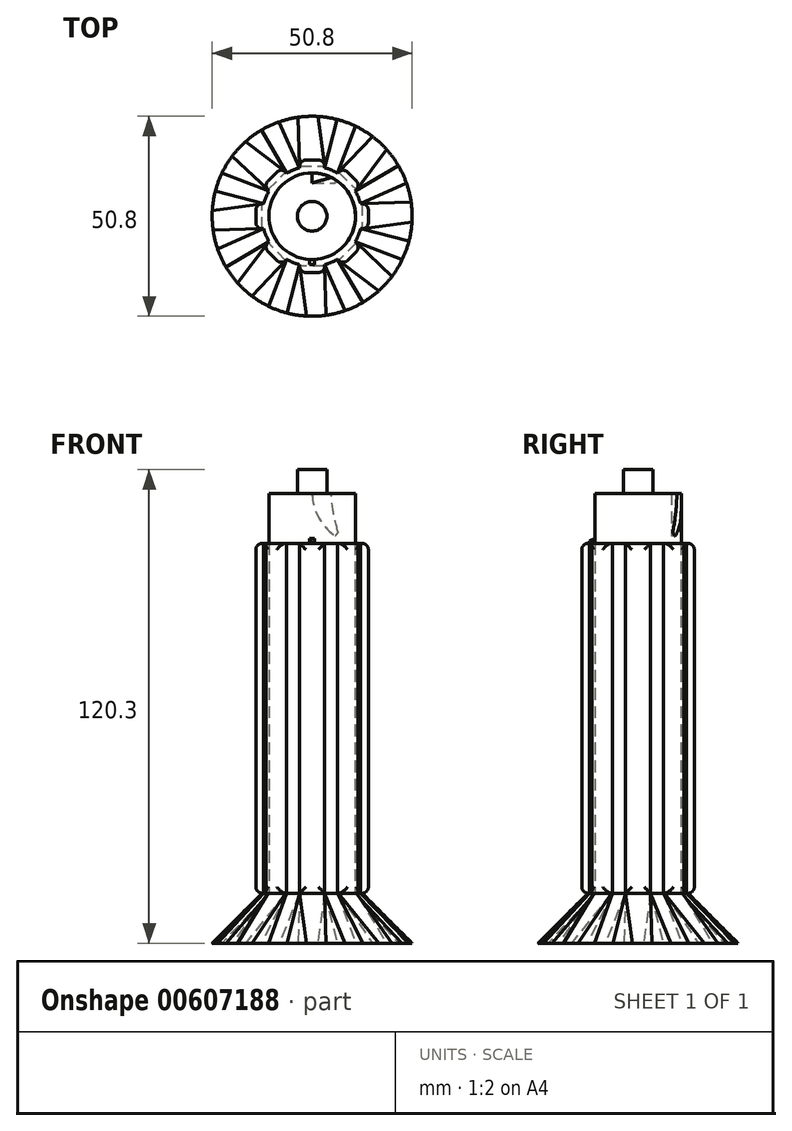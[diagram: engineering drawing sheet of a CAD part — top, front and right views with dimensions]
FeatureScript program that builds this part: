
annotation { "Feature Type Name" : "Feature", "Feature Type Description" : "" }
export const myFeature = defineFeature(function(context is Context, id is Id, definition is map)
    precondition{}
    {
        {
            var Q0;
            Q0=qCreatedBy(makeId("Top.planeOp"),FACE);
            var sketch = newSketch(context, id + "F0", { "sketchPlane" : qUnion([Q0])});
            skCircle(sketch, "E0", {"center": v(0, 0) * mm, "radius": 12.7 * mm});
            skLineSegment(sketch, "E1.bottom", {"start": v(-3.18, 14.29) * mm, "end": v(3.18, 14.29) * mm});
            skLineSegment(sketch, "E1.top", {"start": v(-3.18, 11.11) * mm, "end": v(3.18, 11.11) * mm});
            skLineSegment(sketch, "E1.left", {"start": v(-3.18, 14.29) * mm, "end": v(-3.18, 11.11) * mm});
            skLineSegment(sketch, "E1.right", {"start": v(3.18, 14.29) * mm, "end": v(3.18, 11.11) * mm});
            skLineSegment(sketch, "E2.1.0", {"start": v(-12.35, 7.86) * mm, "end": v(-7.86, 12.35) * mm});
            skLineSegment(sketch, "E2.1.1", {"start": v(-7.86, 12.35) * mm, "end": v(-5.61, 10.1) * mm});
            skLineSegment(sketch, "E2.1.2", {"start": v(-12.35, 7.86) * mm, "end": v(-10.1, 5.61) * mm});
            skLineSegment(sketch, "E2.1.3", {"start": v(-10.1, 5.61) * mm, "end": v(-5.61, 10.1) * mm});
            skLineSegment(sketch, "E2.2.0", {"start": v(-14.29, -3.17) * mm, "end": v(-14.29, 3.18) * mm});
            skLineSegment(sketch, "E2.2.1", {"start": v(-14.29, 3.18) * mm, "end": v(-11.11, 3.18) * mm});
            skLineSegment(sketch, "E2.2.2", {"start": v(-14.29, -3.17) * mm, "end": v(-11.11, -3.17) * mm});
            skLineSegment(sketch, "E2.2.3", {"start": v(-11.11, -3.17) * mm, "end": v(-11.11, 3.18) * mm});
            skLineSegment(sketch, "E2.3.0", {"start": v(-7.86, -12.35) * mm, "end": v(-12.35, -7.86) * mm});
            skLineSegment(sketch, "E2.3.1", {"start": v(-12.35, -7.86) * mm, "end": v(-10.1, -5.61) * mm});
            skLineSegment(sketch, "E2.3.2", {"start": v(-7.86, -12.35) * mm, "end": v(-5.61, -10.1) * mm});
            skLineSegment(sketch, "E2.3.3", {"start": v(-5.61, -10.1) * mm, "end": v(-10.1, -5.61) * mm});
            skLineSegment(sketch, "E2.4.0", {"start": v(3.17, -14.29) * mm, "end": v(-3.18, -14.29) * mm});
            skLineSegment(sketch, "E2.4.1", {"start": v(-3.18, -14.29) * mm, "end": v(-3.18, -11.11) * mm});
            skLineSegment(sketch, "E2.4.2", {"start": v(3.17, -14.29) * mm, "end": v(3.17, -11.11) * mm});
            skLineSegment(sketch, "E2.4.3", {"start": v(3.17, -11.11) * mm, "end": v(-3.18, -11.11) * mm});
            skLineSegment(sketch, "E2.5.0", {"start": v(12.35, -7.86) * mm, "end": v(7.86, -12.35) * mm});
            skLineSegment(sketch, "E2.5.1", {"start": v(7.86, -12.35) * mm, "end": v(5.61, -10.1) * mm});
            skLineSegment(sketch, "E2.5.2", {"start": v(12.35, -7.86) * mm, "end": v(10.1, -5.61) * mm});
            skLineSegment(sketch, "E2.5.3", {"start": v(10.1, -5.61) * mm, "end": v(5.61, -10.1) * mm});
            skLineSegment(sketch, "E2.6.0", {"start": v(14.29, 3.17) * mm, "end": v(14.29, -3.18) * mm});
            skLineSegment(sketch, "E2.6.1", {"start": v(14.29, -3.18) * mm, "end": v(11.11, -3.18) * mm});
            skLineSegment(sketch, "E2.6.2", {"start": v(14.29, 3.17) * mm, "end": v(11.11, 3.17) * mm});
            skLineSegment(sketch, "E2.6.3", {"start": v(11.11, 3.17) * mm, "end": v(11.11, -3.18) * mm});
            skLineSegment(sketch, "E2.7.0", {"start": v(7.86, 12.35) * mm, "end": v(12.35, 7.86) * mm});
            skLineSegment(sketch, "E2.7.1", {"start": v(12.35, 7.86) * mm, "end": v(10.1, 5.61) * mm});
            skLineSegment(sketch, "E2.7.2", {"start": v(7.86, 12.35) * mm, "end": v(5.61, 10.1) * mm});
            skLineSegment(sketch, "E2.7.3", {"start": v(5.61, 10.1) * mm, "end": v(10.1, 5.61) * mm});
            skSolve(sketch);
        }
        {
            var Q0;
            {var subQ5=sQuery(id+"F0.wireOp",EDGE,"E2.1.0");Q0=makeQuery(id+"F0.imprint","IMPRINT",FACE,{"disambiguationData":[TD([[makeQuery(id+"F0.imprint","IMPRINT",EDGE,{"derivedFrom":subQ5}),-1.0]])]});}
            var Q1;
            {var subQ5=sQuery(id+"F0.wireOp",EDGE,"E2.1.3");Q1=makeQuery(id+"F0.imprint","IMPRINT",FACE,{"disambiguationData":[TD([[makeQuery(id+"F0.imprint","IMPRINT",EDGE,{"derivedFrom":subQ5}),1.0]])]});}
            var Q2;
            {var subQ20=sQuery(id+"F0.wireOp",EDGE,"E1.top");Q2=makeQuery(id+"F0.imprint","IMPRINT",FACE,{"disambiguationData":[TD([[makeQuery(id+"F0.imprint","IMPRINT",EDGE,{"derivedFrom":subQ20}),-1.0]])]});}
            var Q3;
            {var subQ5=sQuery(id+"F0.wireOp",EDGE,"E1.top");Q3=makeQuery(id+"F0.imprint","IMPRINT",FACE,{"disambiguationData":[TD([[makeQuery(id+"F0.imprint","IMPRINT",EDGE,{"derivedFrom":subQ5}),1.0]])]});}
            var Q4;
            {var subQ5=sQuery(id+"F0.wireOp",EDGE,"E1.bottom");Q4=makeQuery(id+"F0.imprint","IMPRINT",FACE,{"disambiguationData":[TD([[makeQuery(id+"F0.imprint","IMPRINT",EDGE,{"derivedFrom":subQ5}),-1.0]])]});}
            var Q5;
            {var subQ5=sQuery(id+"F0.wireOp",EDGE,"E2.7.0");Q5=makeQuery(id+"F0.imprint","IMPRINT",FACE,{"disambiguationData":[TD([[makeQuery(id+"F0.imprint","IMPRINT",EDGE,{"derivedFrom":subQ5}),-1.0]])]});}
            var Q6;
            {var subQ5=sQuery(id+"F0.wireOp",EDGE,"E2.7.3");Q6=makeQuery(id+"F0.imprint","IMPRINT",FACE,{"disambiguationData":[TD([[makeQuery(id+"F0.imprint","IMPRINT",EDGE,{"derivedFrom":subQ5}),1.0]])]});}
            var Q7;
            {var subQ5=sQuery(id+"F0.wireOp",EDGE,"E2.6.3");Q7=makeQuery(id+"F0.imprint","IMPRINT",FACE,{"disambiguationData":[TD([[makeQuery(id+"F0.imprint","IMPRINT",EDGE,{"derivedFrom":subQ5}),1.0]])]});}
            var Q8;
            {var subQ5=sQuery(id+"F0.wireOp",EDGE,"E2.6.0");Q8=makeQuery(id+"F0.imprint","IMPRINT",FACE,{"disambiguationData":[TD([[makeQuery(id+"F0.imprint","IMPRINT",EDGE,{"derivedFrom":subQ5}),-1.0]])]});}
            var Q9;
            {var subQ5=sQuery(id+"F0.wireOp",EDGE,"E2.5.3");Q9=makeQuery(id+"F0.imprint","IMPRINT",FACE,{"disambiguationData":[TD([[makeQuery(id+"F0.imprint","IMPRINT",EDGE,{"derivedFrom":subQ5}),1.0]])]});}
            var Q10;
            {var subQ5=sQuery(id+"F0.wireOp",EDGE,"E2.5.0");Q10=makeQuery(id+"F0.imprint","IMPRINT",FACE,{"disambiguationData":[TD([[makeQuery(id+"F0.imprint","IMPRINT",EDGE,{"derivedFrom":subQ5}),-1.0]])]});}
            var Q11;
            {var subQ5=sQuery(id+"F0.wireOp",EDGE,"E2.4.3");Q11=makeQuery(id+"F0.imprint","IMPRINT",FACE,{"disambiguationData":[TD([[makeQuery(id+"F0.imprint","IMPRINT",EDGE,{"derivedFrom":subQ5}),1.0]])]});}
            var Q12;
            {var subQ5=sQuery(id+"F0.wireOp",EDGE,"E2.4.0");Q12=makeQuery(id+"F0.imprint","IMPRINT",FACE,{"disambiguationData":[TD([[makeQuery(id+"F0.imprint","IMPRINT",EDGE,{"derivedFrom":subQ5}),-1.0]])]});}
            var Q13;
            {var subQ5=sQuery(id+"F0.wireOp",EDGE,"E2.3.3");Q13=makeQuery(id+"F0.imprint","IMPRINT",FACE,{"disambiguationData":[TD([[makeQuery(id+"F0.imprint","IMPRINT",EDGE,{"derivedFrom":subQ5}),1.0]])]});}
            var Q14;
            {var subQ5=sQuery(id+"F0.wireOp",EDGE,"E2.3.0");Q14=makeQuery(id+"F0.imprint","IMPRINT",FACE,{"disambiguationData":[TD([[makeQuery(id+"F0.imprint","IMPRINT",EDGE,{"derivedFrom":subQ5}),-1.0]])]});}
            var Q15;
            {var subQ5=sQuery(id+"F0.wireOp",EDGE,"E2.2.3");Q15=makeQuery(id+"F0.imprint","IMPRINT",FACE,{"disambiguationData":[TD([[makeQuery(id+"F0.imprint","IMPRINT",EDGE,{"derivedFrom":subQ5}),1.0]])]});}
            var Q16;
            {var subQ5=sQuery(id+"F0.wireOp",EDGE,"E2.2.0");Q16=makeQuery(id+"F0.imprint","IMPRINT",FACE,{"disambiguationData":[TD([[makeQuery(id+"F0.imprint","IMPRINT",EDGE,{"derivedFrom":subQ5}),-1.0]])]});}
            extrude(context, id + "F1", {"entities" : qUnion([Q0, Q1, Q2, Q3, Q4, Q5, Q6, Q7, Q8, Q9, Q10, Q11, Q12, Q13, Q14, Q15, Q16]), "depth" : 88.9 * mm, "offsetDistance" : 25.4 * mm});
        }
        {
            var Q0;
            Q0=makeQuery(id+"F1.opExtrude","CAP_FACE",FACE,{"disambiguationData":[OSD([sQuery(id+"F0.wireOp",EDGE,"E0"),sQuery(id+"F0.wireOp",EDGE,"E1.bottom"),sQuery(id+"F0.wireOp",EDGE,"E1.left"),sQuery(id+"F0.wireOp",EDGE,"E1.right"),sQuery(id+"F0.wireOp",EDGE,"E2.1.0"),sQuery(id+"F0.wireOp",EDGE,"E2.1.1"),sQuery(id+"F0.wireOp",EDGE,"E2.1.2"),sQuery(id+"F0.wireOp",EDGE,"E2.2.0"),sQuery(id+"F0.wireOp",EDGE,"E2.2.1"),sQuery(id+"F0.wireOp",EDGE,"E2.2.2"),sQuery(id+"F0.wireOp",EDGE,"E2.3.0"),sQuery(id+"F0.wireOp",EDGE,"E2.3.1"),sQuery(id+"F0.wireOp",EDGE,"E2.3.2"),sQuery(id+"F0.wireOp",EDGE,"E2.4.0"),sQuery(id+"F0.wireOp",EDGE,"E2.4.1"),sQuery(id+"F0.wireOp",EDGE,"E2.4.2"),sQuery(id+"F0.wireOp",EDGE,"E2.5.0"),sQuery(id+"F0.wireOp",EDGE,"E2.5.1"),sQuery(id+"F0.wireOp",EDGE,"E2.5.2"),sQuery(id+"F0.wireOp",EDGE,"E2.6.0"),sQuery(id+"F0.wireOp",EDGE,"E2.6.1"),sQuery(id+"F0.wireOp",EDGE,"E2.6.2"),sQuery(id+"F0.wireOp",EDGE,"E2.7.0"),sQuery(id+"F0.wireOp",EDGE,"E2.7.1"),sQuery(id+"F0.wireOp",EDGE,"E2.7.2")])],"isStart":true});
            cPlane(context, id + "F2", {"entities" : qUnion([Q0]), "cplaneType" : CPlaneType.OFFSET, "offset" : 12.7 * mm, "width" : 152.4 * mm, "height" : 152.4 * mm});
        }
        {
            var Q0;
            Q0=qCreatedBy(id+"F2.planeOp",FACE);
            var sketch = newSketch(context, id + "F3", { "sketchPlane" : qUnion([Q0])});
            skCircle(sketch, "E3", {"center": v(0, 0) * mm, "radius": 25.4 * mm});
            skSolve(sketch);
        }
        {
            var Q0;
            Q0=makeQuery(id+"F1.opExtrude","SWEPT_FACE",FACE,{"disambiguationData":[OSD([sQuery(id+"F0.wireOp",EDGE,"E1.bottom")])]});
            var Q1;
            Q1=makeQuery(id+"F1.opExtrude","SWEPT_FACE",FACE,{"disambiguationData":[OSD([sQuery(id+"F0.wireOp",EDGE,"E2.1.0")])]});
            var Q2;
            Q2=makeQuery(id+"F1.opExtrude","SWEPT_FACE",FACE,{"disambiguationData":[OSD([sQuery(id+"F0.wireOp",EDGE,"E2.7.0")])]});
            var Q3;
            Q3=makeQuery(id+"F1.opExtrude","SWEPT_FACE",FACE,{"disambiguationData":[OSD([sQuery(id+"F0.wireOp",EDGE,"E2.6.0")])]});
            var Q4;
            Q4=makeQuery(id+"F1.opExtrude","SWEPT_FACE",FACE,{"disambiguationData":[OSD([sQuery(id+"F0.wireOp",EDGE,"E2.5.0")])]});
            var Q5;
            Q5=makeQuery(id+"F1.opExtrude","SWEPT_FACE",FACE,{"disambiguationData":[OSD([sQuery(id+"F0.wireOp",EDGE,"E2.4.0")])]});
            var Q6;
            Q6=makeQuery(id+"F1.opExtrude","SWEPT_FACE",FACE,{"disambiguationData":[OSD([sQuery(id+"F0.wireOp",EDGE,"E2.3.0")])]});
            var Q7;
            Q7=makeQuery(id+"F1.opExtrude","SWEPT_FACE",FACE,{"disambiguationData":[OSD([sQuery(id+"F0.wireOp",EDGE,"E2.2.0")])]});
            var Q8;
            Q8=makeQuery(id+"F1.opExtrude","CAP_EDGE",EDGE,{"disambiguationData":[OSD([sQuery(id+"F0.wireOp",EDGE,"E2.3.0")])],"isStart":true});
            fillet(context, id + "F4", {"entities" : qUnion([Q0, Q1, Q2, Q3, Q4, Q5, Q6, Q7, Q8]), "radius" : 1.59 * mm, "tangentPropagation" : true, "allowEdgeOverflow" : false});
        }
        {
            var Q1;
            Q1=makeQuery(id+"F1.opExtrude","CAP_FACE",FACE,{"disambiguationData":[OSD([sQuery(id+"F0.wireOp",EDGE,"E0"),sQuery(id+"F0.wireOp",EDGE,"E1.bottom"),sQuery(id+"F0.wireOp",EDGE,"E1.left"),sQuery(id+"F0.wireOp",EDGE,"E1.right"),sQuery(id+"F0.wireOp",EDGE,"E2.1.0"),sQuery(id+"F0.wireOp",EDGE,"E2.1.1"),sQuery(id+"F0.wireOp",EDGE,"E2.1.2"),sQuery(id+"F0.wireOp",EDGE,"E2.2.0"),sQuery(id+"F0.wireOp",EDGE,"E2.2.1"),sQuery(id+"F0.wireOp",EDGE,"E2.2.2"),sQuery(id+"F0.wireOp",EDGE,"E2.3.0"),sQuery(id+"F0.wireOp",EDGE,"E2.3.1"),sQuery(id+"F0.wireOp",EDGE,"E2.3.2"),sQuery(id+"F0.wireOp",EDGE,"E2.4.0"),sQuery(id+"F0.wireOp",EDGE,"E2.4.1"),sQuery(id+"F0.wireOp",EDGE,"E2.4.2"),sQuery(id+"F0.wireOp",EDGE,"E2.5.0"),sQuery(id+"F0.wireOp",EDGE,"E2.5.1"),sQuery(id+"F0.wireOp",EDGE,"E2.5.2"),sQuery(id+"F0.wireOp",EDGE,"E2.6.0"),sQuery(id+"F0.wireOp",EDGE,"E2.6.1"),sQuery(id+"F0.wireOp",EDGE,"E2.6.2"),sQuery(id+"F0.wireOp",EDGE,"E2.7.0"),sQuery(id+"F0.wireOp",EDGE,"E2.7.1"),sQuery(id+"F0.wireOp",EDGE,"E2.7.2")])],"isStart":true});
            var Q2;
            Q2=makeQuery(id+"F3.imprint","IMPRINT",FACE,{"disambiguationData":[TD([[makeQuery(id+"F3.imprint","IMPRINT",EDGE,{"derivedFrom":sQuery(id+"F3.wireOp",EDGE,"E3")}),1.0]])]});
            loft(context, id + "F5", {"operationType" : NewBodyOperationType.ADD, "sheetProfilesArray" : [{ "sheetProfileEntities" : qUnion([Q1]) }, { "sheetProfileEntities" : qUnion([Q2]) }]});
        }
        {
            var Q0;
            Q0=makeQuery(id+"F1.opExtrude","CAP_FACE",FACE,{"disambiguationData":[OSD([sQuery(id+"F0.wireOp",EDGE,"E0"),sQuery(id+"F0.wireOp",EDGE,"E1.bottom"),sQuery(id+"F0.wireOp",EDGE,"E1.left"),sQuery(id+"F0.wireOp",EDGE,"E1.right"),sQuery(id+"F0.wireOp",EDGE,"E2.1.0"),sQuery(id+"F0.wireOp",EDGE,"E2.1.1"),sQuery(id+"F0.wireOp",EDGE,"E2.1.2"),sQuery(id+"F0.wireOp",EDGE,"E2.2.0"),sQuery(id+"F0.wireOp",EDGE,"E2.2.1"),sQuery(id+"F0.wireOp",EDGE,"E2.2.2"),sQuery(id+"F0.wireOp",EDGE,"E2.3.0"),sQuery(id+"F0.wireOp",EDGE,"E2.3.1"),sQuery(id+"F0.wireOp",EDGE,"E2.3.2"),sQuery(id+"F0.wireOp",EDGE,"E2.4.0"),sQuery(id+"F0.wireOp",EDGE,"E2.4.1"),sQuery(id+"F0.wireOp",EDGE,"E2.4.2"),sQuery(id+"F0.wireOp",EDGE,"E2.5.0"),sQuery(id+"F0.wireOp",EDGE,"E2.5.1"),sQuery(id+"F0.wireOp",EDGE,"E2.5.2"),sQuery(id+"F0.wireOp",EDGE,"E2.6.0"),sQuery(id+"F0.wireOp",EDGE,"E2.6.1"),sQuery(id+"F0.wireOp",EDGE,"E2.6.2"),sQuery(id+"F0.wireOp",EDGE,"E2.7.0"),sQuery(id+"F0.wireOp",EDGE,"E2.7.1"),sQuery(id+"F0.wireOp",EDGE,"E2.7.2")])],"isStart":false});
            var sketch = newSketch(context, id + "F6", { "sketchPlane" : qUnion([Q0])});
            skCircle(sketch, "E4", {"center": v(0, 0) * mm, "radius": 11 * mm});
            skSolve(sketch);
        }
        {
            var Q0;
            Q0=makeQuery(id+"F6.imprint","IMPRINT",FACE,{"disambiguationData":[TD([[makeQuery(id+"F6.imprint","IMPRINT",EDGE,{"derivedFrom":sQuery(id+"F6.wireOp",EDGE,"E4")}),1.0]])]});
            extrude(context, id + "F7", {"entities" : qUnion([Q0]), "operationType" : NewBodyOperationType.ADD, "depth" : 12.7 * mm, "offsetDistance" : 25.4 * mm});
        }
        {
            var Q0;
            Q0=makeQuery(id+"F7.opExtrude","CAP_FACE",FACE,{"disambiguationData":[OSD([sQuery(id+"F6.wireOp",EDGE,"E4")])],"isStart":false});
            var sketch = newSketch(context, id + "F8", { "sketchPlane" : qUnion([Q0])});
            skCircle(sketch, "E5", {"center": v(0, 0) * mm, "radius": 3.75 * mm});
            skSolve(sketch);
        }
        {
            var Q0;
            Q0=makeQuery(id+"F8.imprint","IMPRINT",FACE,{"disambiguationData":[TD([[makeQuery(id+"F8.imprint","IMPRINT",EDGE,{"derivedFrom":sQuery(id+"F8.wireOp",EDGE,"E5")}),1.0]])]});
            extrude(context, id + "F9", {"entities" : qUnion([Q0]), "operationType" : NewBodyOperationType.ADD, "depth" : 6 * mm, "offsetDistance" : 25.4 * mm});
        }
        {
            var Q0;
            Q0=makeQuery(id+"F7.opExtrude","CAP_FACE",FACE,{"disambiguationData":[OSD([sQuery(id+"F6.wireOp",EDGE,"E4")])],"isStart":false});
            var sketch = newSketch(context, id + "F10", { "sketchPlane" : qUnion([Q0])});
            skLineSegment(sketch, "E6", {"start": v(0, 11) * mm, "end": v(0, 8.46) * mm});
            skLineSegment(sketch, "E7", {"start": v(0, 8.46) * mm, "end": v(4.88, 9.86) * mm});
            skCircle(sketch, "E8.0", {"center": v(0, 0) * mm, "radius": 11 * mm});
            skSolve(sketch);
        }
        {
            var Q0;
            Q0=qCreatedBy(makeId("Front.planeOp"),FACE);
            cPlane(context, id + "F11", {"entities" : qUnion([Q0]), "cplaneType" : CPlaneType.OFFSET, "offset" : 11 * mm, "oppositeDirection" : true, "width" : 152.4 * mm, "height" : 152.4 * mm});
        }
        {
            var Q0;
            Q0=qCreatedBy(id+"F11.planeOp",FACE);
            var sketch = newSketch(context, id + "F12", { "sketchPlane" : qUnion([Q0])});
            skPoint(sketch, "E9.0", {"position": v(0, 101.6) * mm});
            skArc(sketch, "E10", {"start": v(0, 101.6) * mm, "mid": v(1.64, 95.5) * mm, "end": v(5.85, 90.77) * mm});
            skSolve(sketch);
        }
        {
            var Q0;
            {var subQ0=sQuery(id+"F10.wireOp",EDGE,"E6");Q0=makeQuery(id+"F10.imprint","IMPRINT",FACE,{"disambiguationData":[TD([[makeQuery(id+"F10.imprint","IMPRINT",EDGE,{"derivedFrom":subQ0}),1.0]])]});}
            var Q1;
            Q1=sQuery(id+"F12.wireOp",EDGE,"E10");
            sweep(context, id + "F13", {"operationType" : NewBodyOperationType.REMOVE, "profiles" : qUnion([Q0]), "path" : qUnion([Q1])});
        }
        {
            var Q0;
            Q0=makeQuery(id+"F1.opExtrude","CAP_FACE",FACE,{"disambiguationData":[OSD([sQuery(id+"F0.wireOp",EDGE,"E0"),sQuery(id+"F0.wireOp",EDGE,"E1.bottom"),sQuery(id+"F0.wireOp",EDGE,"E1.left"),sQuery(id+"F0.wireOp",EDGE,"E1.right"),sQuery(id+"F0.wireOp",EDGE,"E2.1.0"),sQuery(id+"F0.wireOp",EDGE,"E2.1.1"),sQuery(id+"F0.wireOp",EDGE,"E2.1.2"),sQuery(id+"F0.wireOp",EDGE,"E2.2.0"),sQuery(id+"F0.wireOp",EDGE,"E2.2.1"),sQuery(id+"F0.wireOp",EDGE,"E2.2.2"),sQuery(id+"F0.wireOp",EDGE,"E2.3.0"),sQuery(id+"F0.wireOp",EDGE,"E2.3.1"),sQuery(id+"F0.wireOp",EDGE,"E2.3.2"),sQuery(id+"F0.wireOp",EDGE,"E2.4.0"),sQuery(id+"F0.wireOp",EDGE,"E2.4.1"),sQuery(id+"F0.wireOp",EDGE,"E2.4.2"),sQuery(id+"F0.wireOp",EDGE,"E2.5.0"),sQuery(id+"F0.wireOp",EDGE,"E2.5.1"),sQuery(id+"F0.wireOp",EDGE,"E2.5.2"),sQuery(id+"F0.wireOp",EDGE,"E2.6.0"),sQuery(id+"F0.wireOp",EDGE,"E2.6.1"),sQuery(id+"F0.wireOp",EDGE,"E2.6.2"),sQuery(id+"F0.wireOp",EDGE,"E2.7.0"),sQuery(id+"F0.wireOp",EDGE,"E2.7.1"),sQuery(id+"F0.wireOp",EDGE,"E2.7.2")])],"isStart":false});
            var sketch = newSketch(context, id + "F14", { "sketchPlane" : qUnion([Q0])});
            skLineSegment(sketch, "E11.bottom", {"start": v(-0.64, -10.98) * mm, "end": v(0.64, -10.98) * mm});
            skLineSegment(sketch, "E11.top", {"start": v(-0.64, -12.32) * mm, "end": v(0.64, -12.32) * mm});
            skLineSegment(sketch, "E11.left", {"start": v(-0.64, -10.98) * mm, "end": v(-0.64, -12.32) * mm});
            skLineSegment(sketch, "E11.right", {"start": v(0.64, -10.98) * mm, "end": v(0.64, -12.32) * mm});
            skSolve(sketch);
        }
        {
            var Q0;
            Q0=makeQuery(id+"F14.imprint","IMPRINT",FACE,{"disambiguationData":[TD([[makeQuery(id+"F14.imprint","IMPRINT",EDGE,{"derivedFrom":sQuery(id+"F14.wireOp",EDGE,"E11.top")}),1.0]])]});
            extrude(context, id + "F15", {"entities" : qUnion([Q0]), "operationType" : NewBodyOperationType.ADD, "depth" : 1.27 * mm, "offsetDistance" : 25.4 * mm});
        }
        {
            var Q0;
            Q0=makeQuery(id+"F15.opExtrude","SWEPT_FACE",FACE,{"disambiguationData":[OSD([sQuery(id+"F14.wireOp",EDGE,"E11.right")])]});
            var sketch = newSketch(context, id + "F16", { "sketchPlane" : qUnion([Q0])});
            skLineSegment(sketch, "E12", {"start": v(-10.98, 90.17) * mm, "end": v(-12.32, 88.9) * mm});
            skSolve(sketch);
        }
        {
            var Q0;
            Q0=makeQuery(id+"F15.opExtrude","SWEPT_FACE",FACE,{"disambiguationData":[OSD([sQuery(id+"F14.wireOp",EDGE,"E11.left")])]});
            var sketch = newSketch(context, id + "F17", { "sketchPlane" : qUnion([Q0])});
            skLineSegment(sketch, "E13", {"start": v(10.98, 90.17) * mm, "end": v(12.32, 89.53) * mm});
            skSolve(sketch);
        }
        {
            var Q1;
            {var subQ0=sQuery(id+"F17.wireOp",EDGE,"E13");Q1=makeQuery(id+"F17.imprint","IMPRINT",FACE,{"disambiguationData":[TD([[makeQuery(id+"F17.imprint","IMPRINT",EDGE,{"derivedFrom":subQ0}),1.0]])]});}
            var Q2;
            Q2=makeQuery(id+"F16.imprint","IMPRINT",FACE,{"disambiguationData":[TD([[makeQuery(id+"F16.imprint","IMPRINT",EDGE,{"derivedFrom":sQuery(id+"F16.wireOp",EDGE,"E12")}),-1.0]])]});
            loft(context, id + "F18", {"operationType" : NewBodyOperationType.REMOVE, "sheetProfilesArray" : [{ "sheetProfileEntities" : qUnion([Q1]) }, { "sheetProfileEntities" : qUnion([Q2]) }]});
        }
    });
